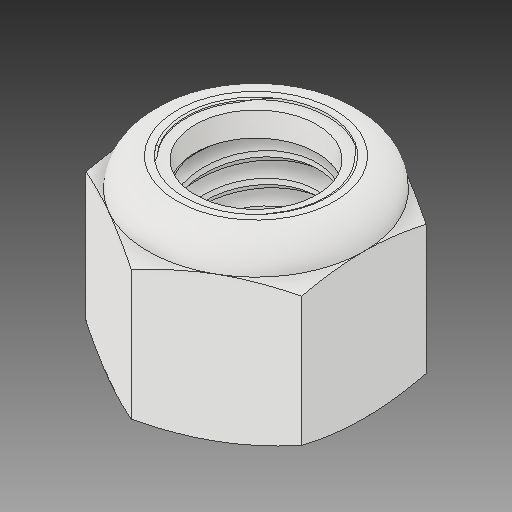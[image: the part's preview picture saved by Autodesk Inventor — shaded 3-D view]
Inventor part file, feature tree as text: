
AUTODESK INVENTOR PART (.ipt)
format: ipt  version: 2018 (Build 220112000, 112)  size: 374,784 bytes
history: native  units: in
note: dims shown in document units (in); Inventor stores cm internally (conversion verified against a paired STEP export)
features: other x1, revolve x1
ambient origin geometry x8: Origin, YZ Plane, XZ Plane, XY Plane, X Axis, Y Axis, Z Axis, Center Point
bodies: Solid1 (feature_tree), Solid2 (feature_tree)
feature tree (2):
  other  "Cut-Revolve4"
  revolve  "Revolve2"  [1 undecoded]
note: 1 required parameter value undecoded (feature->parameter linkage not recoverable at this tier; creation-order binding heuristic only, values carry confidence <= 0.55)
